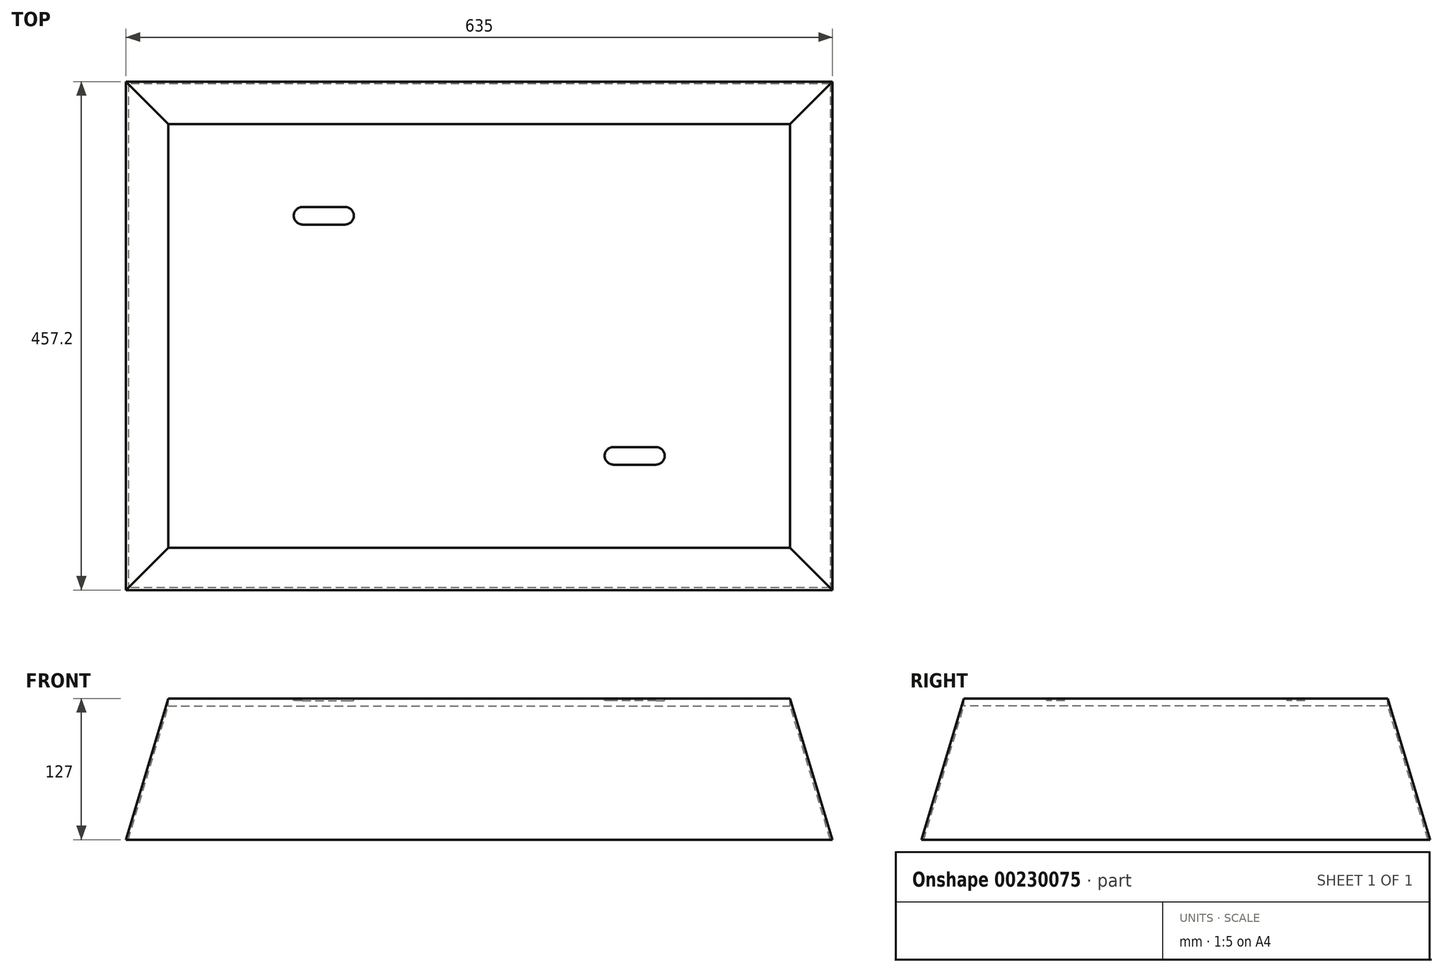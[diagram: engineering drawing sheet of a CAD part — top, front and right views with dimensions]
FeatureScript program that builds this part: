
annotation { "Feature Type Name" : "Feature", "Feature Type Description" : "" }
export const myFeature = defineFeature(function(context is Context, id is Id, definition is map)
    precondition{}
    {
        {
            var Q0;
            Q0=qCreatedBy(makeId("Top.planeOp"),FACE);
            var sketch = newSketch(context, id + "F0", { "sketchPlane" : qUnion([Q0])});
            skLineSegment(sketch, "E0.bottom", {"start": v(317.5, 228.6) * mm, "end": v(-317.5, 228.6) * mm});
            skLineSegment(sketch, "E0.top", {"start": v(317.5, -228.6) * mm, "end": v(-317.5, -228.6) * mm});
            skLineSegment(sketch, "E0.left", {"start": v(317.5, 228.6) * mm, "end": v(317.5, -228.6) * mm});
            skLineSegment(sketch, "E0.right", {"start": v(-317.5, 228.6) * mm, "end": v(-317.5, -228.6) * mm});
            skPoint(sketch, "E0.middle", {"position": v(0, 0) * mm});
            skSolve(sketch);
        }
        {
            var Q0;
            Q0 = qSketchRegion(id + "F0", true);
            extrude(context, id + "F1", {"entities" : qUnion([Q0]), "depth" : 127 * mm});
        }
        {
            var Q0;
            Q0=makeQuery(id+"F1.opExtrude","SWEPT_FACE",FACE,{"disambiguationData":[OSD([sQuery(id+"F0.wireOp",EDGE,"E0.top")])]});
            var sketch = newSketch(context, id + "F2", { "sketchPlane" : qUnion([Q0])});
            skLineSegment(sketch, "E1", {"start": v(317.5, 0) * mm, "end": v(279.4, 127) * mm});
            skLineSegment(sketch, "E2", {"start": v(279.4, 127) * mm, "end": v(317.5, 127) * mm});
            skLineSegment(sketch, "E3", {"start": v(317.5, 127) * mm, "end": v(317.5, 0) * mm});
            skLineSegment(sketch, "E4.MirrorCS", {"start": v(-279.4, 127) * mm, "end": v(-317.5, 127) * mm});
            skLineSegment(sketch, "E5.MirrorCS", {"start": v(-317.5, 0) * mm, "end": v(-279.4, 127) * mm});
            skLineSegment(sketch, "E6.MirrorCS", {"start": v(-317.5, 127) * mm, "end": v(-317.5, 0) * mm});
            skSolve(sketch);
        }
        {
            var Q0;
            Q0=makeQuery(id+"F2.imprint","IMPRINT",FACE,{"disambiguationData":[TD([[makeQuery(id+"F2.imprint","IMPRINT",EDGE,{"derivedFrom":sQuery(id+"F2.wireOp",EDGE,"E4.MirrorCS")}),1.0]])]});
            var Q1;
            Q1=makeQuery(id+"F2.imprint","IMPRINT",FACE,{"disambiguationData":[TD([[makeQuery(id+"F2.imprint","IMPRINT",EDGE,{"derivedFrom":sQuery(id+"F2.wireOp",EDGE,"E1")}),-1.0]])]});
            extrude(context, id + "F3", {"entities" : qUnion([Q0, Q1]), "operationType" : NewBodyOperationType.REMOVE, "endBound" : BoundingType.THROUGH_ALL, "oppositeDirection" : true, "depth" : 25.4 * mm});
        }
        {
            var Q0;
            Q0=qCreatedBy(makeId("Right.planeOp"),FACE);
            var sketch = newSketch(context, id + "F4", { "sketchPlane" : qUnion([Q0])});
            skLineSegment(sketch, "E7", {"start": v(-228.6, 0) * mm, "end": v(-228.6, 127) * mm});
            skLineSegment(sketch, "E8", {"start": v(-228.6, 127) * mm, "end": v(-190.5, 127) * mm});
            skLineSegment(sketch, "E9", {"start": v(-190.5, 127) * mm, "end": v(-228.6, 0) * mm});
            skLineSegment(sketch, "E10.MirrorCS", {"start": v(228.6, 127) * mm, "end": v(190.5, 127) * mm});
            skLineSegment(sketch, "E11.MirrorCS", {"start": v(228.6, 0) * mm, "end": v(228.6, 127) * mm});
            skLineSegment(sketch, "E12.MirrorCS", {"start": v(190.5, 127) * mm, "end": v(228.6, 0) * mm});
            skSolve(sketch);
        }
        {
            var Q0;
            Q0 = qSketchRegion(id + "F4", true);
            extrude(context, id + "F5", {"entities" : qUnion([Q0]), "operationType" : NewBodyOperationType.REMOVE, "endBound" : BoundingType.SYMMETRIC, "depth" : 660.4 * mm});
        }
        {
            var Q0;
            Q0=makeQuery(id+"F1.opExtrude","CAP_FACE",FACE,{"disambiguationData":[OSD([sQuery(id+"F0.wireOp",EDGE,"E0.bottom"),sQuery(id+"F0.wireOp",EDGE,"E0.top"),sQuery(id+"F0.wireOp",EDGE,"E0.left"),sQuery(id+"F0.wireOp",EDGE,"E0.right")])],"isStart":true});
            shell(context, id + "F6", {"entities" : qUnion([Q0]), "thickness" : 1.93 * mm});
        }
        {
            var Q0;
            Q0=makeQuery(id+"F1.opExtrude","CAP_FACE",FACE,{"disambiguationData":[OSD([sQuery(id+"F0.wireOp",EDGE,"E0.bottom"),sQuery(id+"F0.wireOp",EDGE,"E0.top"),sQuery(id+"F0.wireOp",EDGE,"E0.left"),sQuery(id+"F0.wireOp",EDGE,"E0.right")])],"isStart":false});
            var sketch = newSketch(context, id + "F7", { "sketchPlane" : qUnion([Q0])});
            skLineSegment(sketch, "E13", {"start": v(-158.75, 107.95) * mm, "end": v(-120.65, 107.95) * mm, "construction": true});
            skArc(sketch, "E14.0.startCap", {"start": v(-158.75, 100.01) * mm, "mid": v(-166.69, 107.95) * mm, "end": v(-158.75, 115.89) * mm});
            skArc(sketch, "E14.0.endCap", {"start": v(-120.65, 115.89) * mm, "mid": v(-112.71, 107.95) * mm, "end": v(-120.65, 100.01) * mm});
            skLineSegment(sketch, "E14.0.left", {"start": v(-158.75, 115.89) * mm, "end": v(-120.65, 115.89) * mm});
            skLineSegment(sketch, "E14.0.right", {"start": v(-158.75, 100.01) * mm, "end": v(-120.65, 100.01) * mm});
            skLineSegment(sketch, "E15", {"start": v(-139.7, 107.95) * mm, "end": v(-139.7, 147.68) * mm, "construction": true});
            skLineSegment(sketch, "E16", {"start": v(0, 0) * mm, "end": v(0, 281.86) * mm, "construction": true});
            skLineSegment(sketch, "E17.MirrorCS", {"start": v(158.75, 115.89) * mm, "end": v(120.65, 115.89) * mm});
            skArc(sketch, "E18.MirrorCS", {"start": v(158.75, 100.01) * mm, "mid": v(166.69, 107.95) * mm, "end": v(158.75, 115.89) * mm});
            skLineSegment(sketch, "E19.MirrorCS", {"start": v(158.75, 100.01) * mm, "end": v(120.65, 100.01) * mm});
            skArc(sketch, "E20.MirrorCS", {"start": v(120.65, 115.89) * mm, "mid": v(112.71, 107.95) * mm, "end": v(120.65, 100.01) * mm});
            skLineSegment(sketch, "E21", {"start": v(0, 0) * mm, "end": v(116.98, 0) * mm, "construction": true});
            skLineSegment(sketch, "E22", {"start": v(0, 57.15) * mm, "end": v(119.38, 57.15) * mm, "construction": true});
            skLineSegment(sketch, "E23.MirrorCS", {"start": v(-158.75, 6.35) * mm, "end": v(-120.65, 6.35) * mm, "construction": true});
            skArc(sketch, "E24.MirrorCS", {"start": v(-120.65, -1.59) * mm, "mid": v(-112.71, 6.35) * mm, "end": v(-120.65, 14.29) * mm});
            skLineSegment(sketch, "E25.MirrorCS", {"start": v(-158.75, -1.59) * mm, "end": v(-120.65, -1.59) * mm});
            skLineSegment(sketch, "E26.MirrorCS", {"start": v(-158.75, 14.29) * mm, "end": v(-120.65, 14.29) * mm});
            skLineSegment(sketch, "E27.MirrorCS", {"start": v(158.75, -1.59) * mm, "end": v(120.65, -1.59) * mm});
            skArc(sketch, "E28.MirrorCS", {"start": v(158.75, 14.29) * mm, "mid": v(166.69, 6.35) * mm, "end": v(158.75, -1.59) * mm});
            skLineSegment(sketch, "E29.MirrorCS", {"start": v(158.75, 14.29) * mm, "end": v(120.65, 14.29) * mm});
            skArc(sketch, "E30.MirrorCS", {"start": v(120.65, -1.59) * mm, "mid": v(112.71, 6.35) * mm, "end": v(120.65, 14.29) * mm});
            skArc(sketch, "E31.MirrorCS", {"start": v(-158.75, 14.29) * mm, "mid": v(-166.69, 6.35) * mm, "end": v(-158.75, -1.59) * mm});
            skLineSegment(sketch, "E32.MirrorCS", {"start": v(-158.75, -115.89) * mm, "end": v(-120.65, -115.89) * mm});
            skLineSegment(sketch, "E33.MirrorCS", {"start": v(-158.75, -100.01) * mm, "end": v(-120.65, -100.01) * mm});
            skArc(sketch, "E34.MirrorCS", {"start": v(-120.65, -115.89) * mm, "mid": v(-112.71, -107.95) * mm, "end": v(-120.65, -100.01) * mm});
            skArc(sketch, "E35.MirrorCS", {"start": v(120.65, -115.89) * mm, "mid": v(112.71, -107.95) * mm, "end": v(120.65, -100.01) * mm});
            skLineSegment(sketch, "E36.MirrorCS", {"start": v(158.75, -100.01) * mm, "end": v(120.65, -100.01) * mm});
            skArc(sketch, "E37.MirrorCS", {"start": v(158.75, -100.01) * mm, "mid": v(166.69, -107.95) * mm, "end": v(158.75, -115.89) * mm});
            skLineSegment(sketch, "E38.MirrorCS", {"start": v(158.75, -115.89) * mm, "end": v(120.65, -115.89) * mm});
            skArc(sketch, "E39.MirrorCS", {"start": v(-158.75, -100.01) * mm, "mid": v(-166.69, -107.95) * mm, "end": v(-158.75, -115.89) * mm});
            skLineSegment(sketch, "E40.MirrorCS", {"start": v(-158.75, -107.95) * mm, "end": v(-120.65, -107.95) * mm, "construction": true});
            skSolve(sketch);
        }
        {
            var Q0;
            Q0=makeQuery(id+"F7.imprint","IMPRINT",FACE,{"disambiguationData":[TD([[makeQuery(id+"F7.imprint","IMPRINT",EDGE,{"derivedFrom":sQuery(id+"F7.wireOp",EDGE,"E14.0.startCap")}),-1.0]])]});
            var Q1;
            Q1=makeQuery(id+"F7.imprint","IMPRINT",FACE,{"disambiguationData":[TD([[makeQuery(id+"F7.imprint","IMPRINT",EDGE,{"derivedFrom":sQuery(id+"F7.wireOp",EDGE,"E17.MirrorCS")}),1.0]])]});
            var Q2;
            Q2=makeQuery(id+"F7.imprint","IMPRINT",FACE,{"disambiguationData":[TD([[makeQuery(id+"F7.imprint","IMPRINT",EDGE,{"derivedFrom":sQuery(id+"F7.wireOp",EDGE,"E27.MirrorCS")}),-1.0]])]});
            var Q3;
            Q3=makeQuery(id+"F7.imprint","IMPRINT",FACE,{"disambiguationData":[TD([[makeQuery(id+"F7.imprint","IMPRINT",EDGE,{"derivedFrom":sQuery(id+"F7.wireOp",EDGE,"E24.MirrorCS")}),1.0]])]});
            var Q4;
            Q4=makeQuery(id+"F7.imprint","IMPRINT",FACE,{"disambiguationData":[TD([[makeQuery(id+"F7.imprint","IMPRINT",EDGE,{"derivedFrom":sQuery(id+"F7.wireOp",EDGE,"E32.MirrorCS")}),1.0]])]});
            var Q5;
            Q5=makeQuery(id+"F7.imprint","IMPRINT",FACE,{"disambiguationData":[TD([[makeQuery(id+"F7.imprint","IMPRINT",EDGE,{"derivedFrom":sQuery(id+"F7.wireOp",EDGE,"E35.MirrorCS")}),-1.0]])]});
            extrude(context, id + "F8", {"entities" : qUnion([Q0, Q1, Q2, Q3, Q4, Q5]), "operationType" : NewBodyOperationType.REMOVE, "endBound" : BoundingType.THROUGH_ALL, "oppositeDirection" : true, "depth" : 25.4 * mm});
        }
    });
